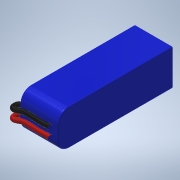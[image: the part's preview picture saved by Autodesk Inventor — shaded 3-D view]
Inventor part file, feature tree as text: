
AUTODESK INVENTOR PART (.ipt)
format: ipt  version: 2020.2 (Build 242310000, 310)  size: 237,056 bytes
history: native  units: mm
features: fillet x2, sketch x2, extrude x1, plane x1, sweep x1, mirror x1
ambient origin geometry x8: Origin, YZ Plane, XZ Plane, XY Plane, X Axis, Y Axis, Z Axis, Center Point
bodies: Volumenkörper1 (feature_tree)
feature tree (8):
  extrude  "Extrusion1"  Depth=105.0mm
  fillet  "Rundung1"  Radius=33.0mm
  plane  "Arbeitsebene4"
  fillet  "Rundung2"  Radius=10.0mm
  sweep  "Sweeping4"
  mirror  "Spiegeln3"
  sketch  "Skizze1"  dims[d0=35.0mm d2=105.0mm d3=33.0mm d4=0.0mm d5=10.0mm]
  sketch  "Skizze10"  dims[d26=4.0mm d33=1.0mm d38=75.0deg d40=3.0mm d42=4.0mm d43=1.0mm d44=0.0mm d45=0.0mm d46=21.942367mm d47=62.217244mm d48=85.487697mm d49=3.954561mm d50=5.563691mm d51=2.46503mm d52=9.958042mm d53=17.398275mm d54=2.832838mm d55=30.542458mm d56=24.526384mm d57=2.648891mm d58=52.5mm d59=17.0mm d60=2.648891mm d61=6.416404mm d62=3.103026mm]
